# Revit family: CADS_AIRFLOWdev_AirflexPro_Grilles_Extract
name_source: partatom
category: Air Terminals
revit_build: Autodesk Revit 2015 (Build: 20160512_1515(x64)
units: mm (PartAtom-declared; Revit-internal decimal feet)

## types (7) — shared parameters
6MonthlyMaintenance = Visually inspect system, clean the fan and ducting if necessary
AssemblyPlace = UNKNOWN
AssetType = FIXED
CEApproval = Yes
Color = Silver
Default Elevation = 1219 mm
DurationUnit = Year
ExpectedServiceLife = 10
Finish = Lacquer
FireControlPanelLinks = No
Fitting Type = Ignore
ISO140001 = Yes
ISO90001 = Yes
IsExtendedWarranty = No
Manufacturer = Airflow Developments Ltd
ManufacturerAddress = Aidelle House
Lancaster Road
Cressex Business Park
High Wycombe
Bucks
HP123QP
ManufacturerTelephone = 01494 525252
ManufacturerWebsite = www.airflow.com
Material = Steel
NBSCode = 90-75-50/370 Air terminals;
PassiveHouseApproval = No
PointOfContact = Airflow Developments Ltd
ProductLiterature = https://www.airflow.com
ProductionYear = 2017
Quantity = 1
RedDotDesignAward = No
SAPApproval = Yes
ServiceLifeDuration = 10
ServiceLifeType = EXPECTEDSERVICELIFE
Shape = Rectangular
Status = New
TemperatureRange = up to 40°C
WarrantyGuarantor = Airflow Developments Ltd
WarrantyPeriod = 0
zero-valued in all types: CADS_Index

## per-type parameters (varying)
| type | Constituents | Features | Grade | GrilleFinish | GrossWeight | L1 | L2 | NominalHeight | NominalLength | NominalWidth | OuterEdge | ReplacementCost | ShippingWeight | Size | Slotted | Squared | Uniclass2015 | Wavey |
| Slotted White Powder Coated | Slotted White Powder Coated Grilles | Slotted White Powder Coated Grilles | White Powder Coated | CADS_AIRFLOWdev_White | 0.78 kg | 143 mm | 342 mm  [stored 1.12205 ft] | 15 mm  [stored 0.0492126 ft] | 342 mm  [stored 1.12205 ft] | 143 mm | No | 107.46 | 0.94 kg | 342 x 143 x 15 | Yes | No | Pr_65_70_46_01 | No |
| Squared White Powder Coated | Squared White Powder Coated Grilles | Squared White Powder Coated Grilles | White Powder Coated | CADS_AIRFLOWdev_White | 0.70 kg | 143 mm | 342 mm  [stored 1.12205 ft] | 15 mm  [stored 0.0492126 ft] | 342 mm  [stored 1.12205 ft] | 143 mm | No | 147.756 | 0.84 kg | 342 x 143 x 15 | No | Yes | Pr_65_70_46_02 | No |
| Wavy White Powder Coated | Wavy White Powder Coated Grilles | Wavy White Powder Coated Grilles | White Powder Coated | CADS_AIRFLOWdev_White | 0.78 kg | 143 mm | 342 mm  [stored 1.12205 ft] | 15 mm  [stored 0.0492126 ft] | 342 mm  [stored 1.12205 ft] | 143 mm | No | 157.608 | 0.94 kg | 342 x 143 x 15 | No | No | Pr_65_70_46_03 | Yes |
| Slotted Brushed Stainless Steel | Slotted Brushed Stainless Steel Grilles | Slotted Brushed Stainless Steel Grilles | Stainless | CADS_AIRFLOWdev_StainlessSteel | 0.78 kg | 143 mm | 342 mm  [stored 1.12205 ft] | 15 mm  [stored 0.0492126 ft] | 342 mm  [stored 1.12205 ft] | 143 mm | No | 122.184 | 0.94 kg | 342 x 143 x 15 | Yes | No | Pr_65_70_46_04 | No |
| Squared Brushed Stainless Steel | Squared Brushed Stainless Steel Grilles | Squared Brushed Stainless Steel Grilles | Stainless | CADS_AIRFLOWdev_StainlessSteel | 0.78 kg | 143 mm | 342 mm  [stored 1.12205 ft] | 15 mm  [stored 0.0492126 ft] | 342 mm  [stored 1.12205 ft] | 143 mm | No | 162.528 | 0.94 kg | 342 x 143 x 15 | No | Yes | Pr_65_70_46_05 | No |
| Wavy Brushed Stainless Steel | Wavy Brushed Stainless Steel Grilles | Wavy Brushed Stainless Steel Grilles | Stainless | CADS_AIRFLOWdev_StainlessSteel | 0.78 kg | 143 mm | 342 mm  [stored 1.12205 ft] | 15 mm  [stored 0.0492126 ft] | 342 mm  [stored 1.12205 ft] | 143 mm | No | 172.344 | 0.94 kg | 342 x 143 x 15 | No | No | Pr_65_70_46_06 | Yes |
| Brushed Stainless Steel Floor | Brushed Stainless Steel Floor Grille | Brushed Stainless Steel Floor Grille | Stainless | CADS_AIRFLOWdev_StainlessSteel | 1.15 kg | 177 mm  [stored 0.580709 ft] | 377 mm  [stored 1.23688 ft] | 65 mm  [stored 0.213255 ft] | 380 mm | 178 mm  [stored 0.58399 ft] | Yes | 218.232 | 1.38 kg | 380 x 178 x 30-65 | No | No | Pr_65_70_46_07 | No |

note: [stored X ft] marks values corroborated as IEEE doubles in the binary element streams (Revit-internal decimal feet)

## geometry (parser evidence)
native form markers: Sweep x6
no freeform markers — native parametric forms only
